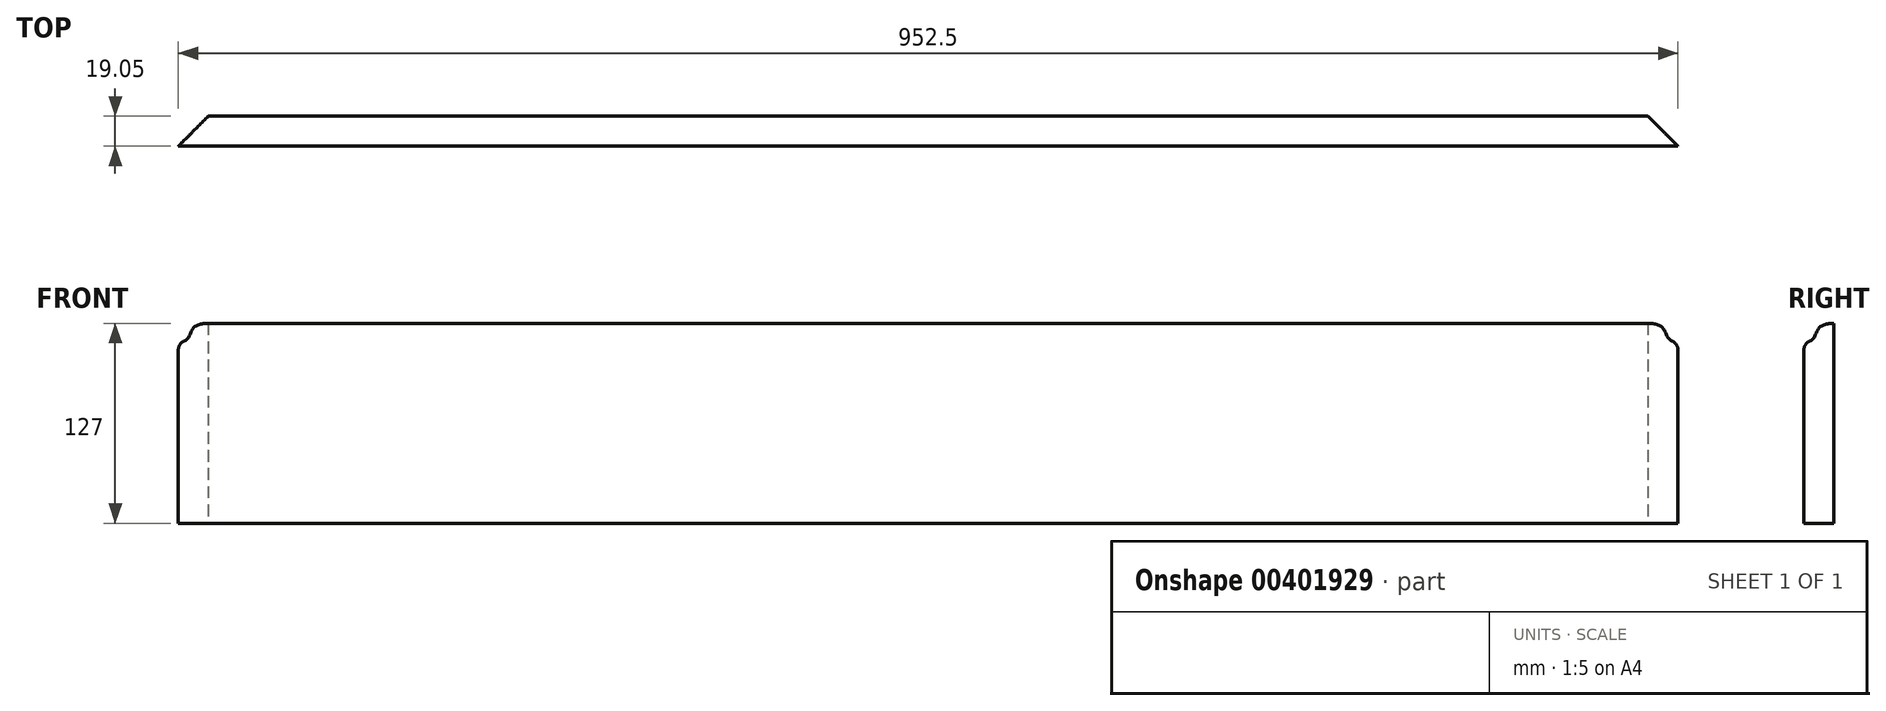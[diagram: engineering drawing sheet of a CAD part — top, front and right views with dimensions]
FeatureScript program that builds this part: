
annotation { "Feature Type Name" : "Feature", "Feature Type Description" : "" }
export const myFeature = defineFeature(function(context is Context, id is Id, definition is map)
    precondition{}
    {
        {
            var Q0;
            Q0=qCreatedBy(makeId("Front.planeOp"),FACE);
            var sketch = newSketch(context, id + "F0", { "sketchPlane" : qUnion([Q0])});
            skLineSegment(sketch, "E0.bottom", {"start": v(476.25, -63.5) * mm, "end": v(-476.25, -63.5) * mm});
            skLineSegment(sketch, "E0.top", {"start": v(476.25, 63.5) * mm, "end": v(-476.25, 63.5) * mm});
            skLineSegment(sketch, "E0.left", {"start": v(476.25, -63.5) * mm, "end": v(476.25, 63.5) * mm});
            skLineSegment(sketch, "E0.right", {"start": v(-476.25, -63.5) * mm, "end": v(-476.25, 63.5) * mm});
            skPoint(sketch, "E0.middle", {"position": v(0, 0) * mm});
            skSolve(sketch);
        }
        {
            var Q0;
            Q0=qSketchRegion(id+"F0",true);
            extrude(context, id + "F1", {"entities" : qUnion([Q0]), "depth" : 19.05 * mm});
        }
        {
            var Q0;
            Q0=makeQuery(id+"F1.opExtrude","SWEPT_FACE",FACE,{"disambiguationData":[OSD([sQuery(id+"F0.wireOp",EDGE,"E0.left")])]});
            var sketch = newSketch(context, id + "F2", { "sketchPlane" : qUnion([Q0])});
            skFitSpline(sketch, "E1", {"points": [v(0, 63.5) * mm, v(-19.05, 51.53) * mm], "startDerivative": vector(-48.08, 0) * mm, "endDerivative": vector(-35.63, -1.9) * mm});
            skArc(sketch, "E2.filletArc", {"start": v(-15.26, 52.32) * mm, "mid": v(-18.02, 49.98) * mm, "end": v(-19.05, 46.5) * mm});
            skLineSegment(sketch, "E3", {"start": v(0, 63.5) * mm, "end": v(-19.05, 63.5) * mm});
            skLineSegment(sketch, "E4", {"start": v(-19.05, 63.5) * mm, "end": v(-19.05, 46.5) * mm});
            skSolve(sketch);
        }
        {
            var Q0;
            Q0=qSketchRegion(id+"F2",true);
            extrude(context, id + "F3", {"entities" : qUnion([Q0]), "operationType" : NewBodyOperationType.REMOVE, "endBound" : BoundingType.THROUGH_ALL, "oppositeDirection" : true, "depth" : 25.4 * mm});
        }
        {
            var Q0;
            Q0=makeQuery(id+"F1.opExtrude","SWEPT_FACE",FACE,{"disambiguationData":[OSD([sQuery(id+"F0.wireOp",EDGE,"E0.bottom")])]});
            var sketch = newSketch(context, id + "F4", { "sketchPlane" : qUnion([Q0])});
            skLineSegment(sketch, "E5", {"start": v(-476.25, 19.05) * mm, "end": v(-476.25, 0) * mm});
            skLineSegment(sketch, "E6", {"start": v(0, 19.05) * mm, "end": v(0, 0) * mm, "construction": true});
            skLineSegment(sketch, "E7", {"start": v(-476.25, 0) * mm, "end": v(-457.2, 0) * mm});
            skLineSegment(sketch, "E8", {"start": v(-457.2, 0) * mm, "end": v(-476.25, 19.05) * mm});
            skLineSegment(sketch, "E9.MirrorCS", {"start": v(457.2, 0) * mm, "end": v(476.25, 19.05) * mm});
            skLineSegment(sketch, "E10.MirrorCS", {"start": v(476.25, 19.05) * mm, "end": v(476.25, 0) * mm});
            skLineSegment(sketch, "E11.MirrorCS", {"start": v(476.25, 0) * mm, "end": v(457.2, 0) * mm});
            skSolve(sketch);
        }
        {
            var Q0;
            Q0=qSketchRegion(id+"F4",true);
            extrude(context, id + "F5", {"entities" : qUnion([Q0]), "operationType" : NewBodyOperationType.REMOVE, "endBound" : BoundingType.THROUGH_ALL, "oppositeDirection" : true, "depth" : 25.4 * mm});
        }
    });
